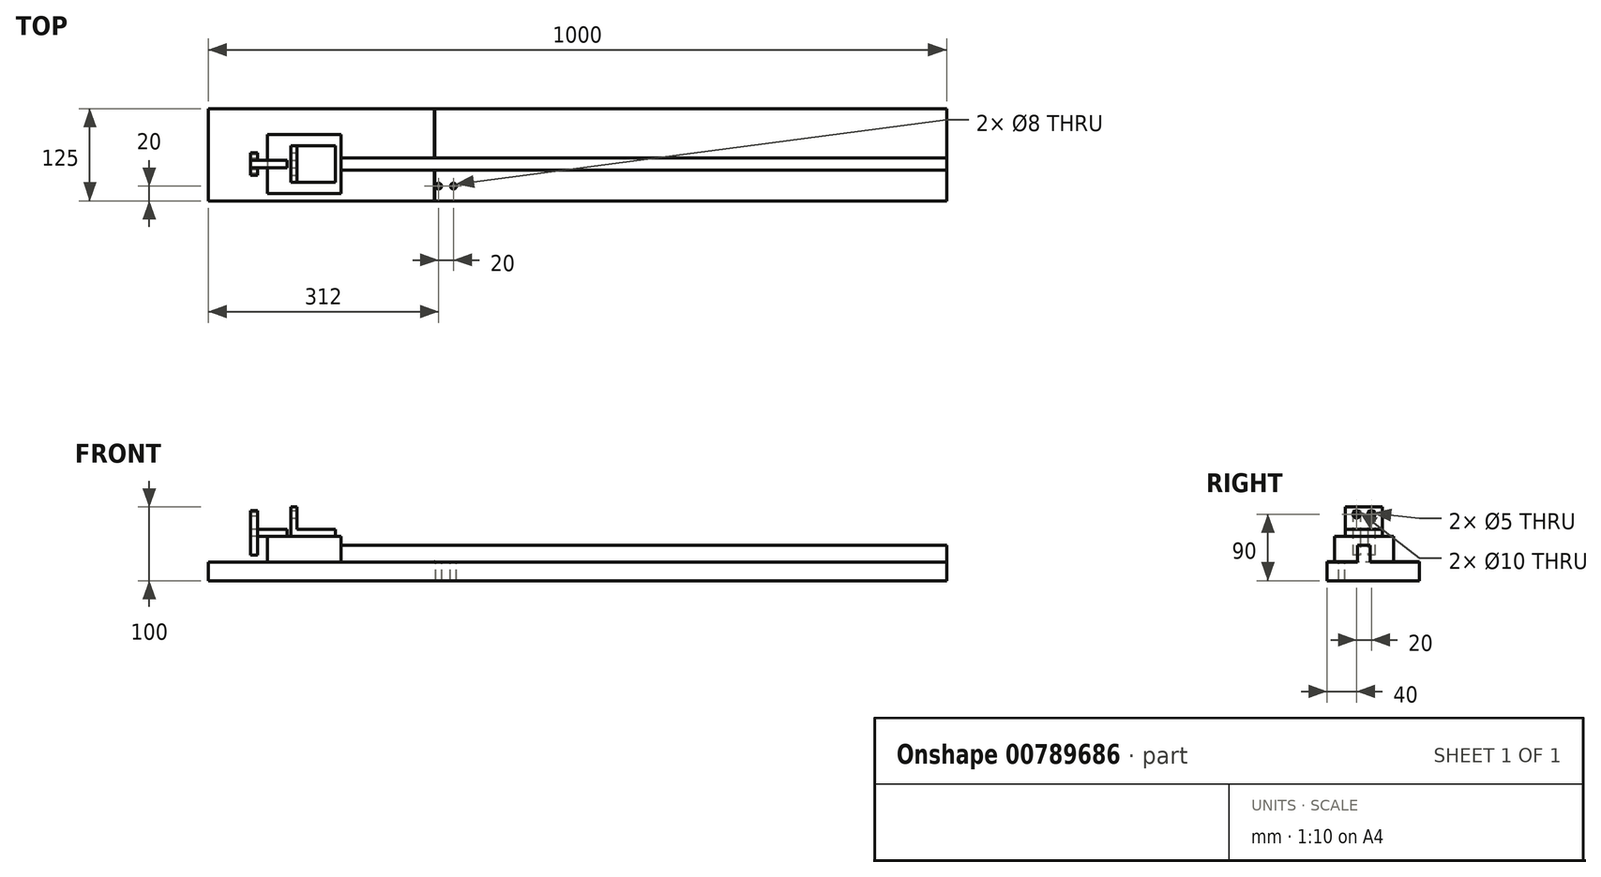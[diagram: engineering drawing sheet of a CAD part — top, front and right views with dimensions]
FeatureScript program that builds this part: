
annotation { "Feature Type Name" : "Feature", "Feature Type Description" : "" }
export const myFeature = defineFeature(function(context is Context, id is Id, definition is map)
    precondition{}
    {
        {
            var Q0;
            Q0=qCreatedBy(makeId("Top.planeOp"),FACE);
            var sketch = newSketch(context, id + "F0", { "sketchPlane" : qUnion([Q0])});
            skLineSegment(sketch, "E0.bottom", {"start": v(0, 0) * mm, "end": v(1000, 0) * mm});
            skLineSegment(sketch, "E0.top", {"start": v(0, 125) * mm, "end": v(1000, 125) * mm});
            skLineSegment(sketch, "E0.left", {"start": v(0, 0) * mm, "end": v(0, 125) * mm});
            skLineSegment(sketch, "E0.right", {"start": v(1000, 0) * mm, "end": v(1000, 125) * mm});
            skSolve(sketch);
        }
        {
            var Q0;
            Q0 = qSketchRegion(id + "F0", true);
            extrude(context, id + "F1", {"entities" : qUnion([Q0]), "depth" : 25 * mm, "offsetDistance" : 25 * mm});
        }
        {
            var Q0;
            Q0=makeQuery(id+"F1.opExtrude","CAP_FACE",FACE,{"disambiguationData":[OSD([sQuery(id+"F0.wireOp",EDGE,"E0.bottom"),sQuery(id+"F0.wireOp",EDGE,"E0.top"),sQuery(id+"F0.wireOp",EDGE,"E0.left"),sQuery(id+"F0.wireOp",EDGE,"E0.right")])],"isStart":false});
            var sketch = newSketch(context, id + "F2", { "sketchPlane" : qUnion([Q0])});
            skLineSegment(sketch, "E1.bottom", {"start": v(180, 41.5) * mm, "end": v(1000, 41.5) * mm});
            skLineSegment(sketch, "E1.top", {"start": v(180, 58.5) * mm, "end": v(1000, 58.5) * mm});
            skLineSegment(sketch, "E1.left", {"start": v(180, 41.5) * mm, "end": v(180, 58.5) * mm});
            skLineSegment(sketch, "E1.right", {"start": v(1000, 41.5) * mm, "end": v(1000, 58.5) * mm});
            skSolve(sketch);
        }
        {
            var Q0;
            Q0 = qSketchRegion(id + "F2", true);
            extrude(context, id + "F3", {"entities" : qUnion([Q0]), "operationType" : NewBodyOperationType.ADD, "depth" : 23 * mm, "offsetDistance" : 25 * mm});
        }
        {
            var Q0;
            Q0=makeQuery(id+"F1.opExtrude","CAP_FACE",FACE,{"disambiguationData":[OSD([sQuery(id+"F0.wireOp",EDGE,"E0.bottom"),sQuery(id+"F0.wireOp",EDGE,"E0.top"),sQuery(id+"F0.wireOp",EDGE,"E0.left"),sQuery(id+"F0.wireOp",EDGE,"E0.right")])],"isStart":false});
            var sketch = newSketch(context, id + "F4", { "sketchPlane" : qUnion([Q0])});
            skCircle(sketch, "E2", {"center": v(312, 20) * mm, "radius": 4 * mm});
            skCircle(sketch, "E3", {"center": v(332, 20) * mm, "radius": 4 * mm});
            skSolve(sketch);
        }
        {
            var Q0;
            Q0 = qSketchRegion(id + "F4", true);
            extrude(context, id + "F5", {"entities" : qUnion([Q0]), "operationType" : NewBodyOperationType.REMOVE, "endBound" : BoundingType.UP_TO_NEXT, "oppositeDirection" : true, "depth" : 25 * mm, "offsetDistance" : 25 * mm});
        }
        {
            var Q0;
            Q0=makeQuery(id+"F1.opExtrude","CAP_FACE",FACE,{"disambiguationData":[OSD([sQuery(id+"F0.wireOp",EDGE,"E0.bottom"),sQuery(id+"F0.wireOp",EDGE,"E0.top"),sQuery(id+"F0.wireOp",EDGE,"E0.left"),sQuery(id+"F0.wireOp",EDGE,"E0.right")])],"isStart":false});
            var sketch = newSketch(context, id + "F6", { "sketchPlane" : qUnion([Q0])});
            skLineSegment(sketch, "E4.bottom", {"start": v(80, 90) * mm, "end": v(180, 90) * mm});
            skLineSegment(sketch, "E4.top", {"start": v(80, 10) * mm, "end": v(180, 10) * mm});
            skLineSegment(sketch, "E4.left", {"start": v(80, 90) * mm, "end": v(80, 10) * mm});
            skLineSegment(sketch, "E4.right", {"start": v(180, 90) * mm, "end": v(180, 10) * mm});
            skSolve(sketch);
        }
        {
            var Q0;
            Q0 = qSketchRegion(id + "F6", true);
            extrude(context, id + "F7", {"entities" : qUnion([Q0]), "operationType" : NewBodyOperationType.ADD, "depth" : 35 * mm, "offsetDistance" : 25 * mm});
        }
        {
            var Q0;
            Q0=makeQuery(id+"F7.opExtrude","CAP_FACE",FACE,{"disambiguationData":[OSD([sQuery(id+"F6.wireOp",EDGE,"E4.bottom"),sQuery(id+"F6.wireOp",EDGE,"E4.top"),sQuery(id+"F6.wireOp",EDGE,"E4.left"),sQuery(id+"F6.wireOp",EDGE,"E4.right")])],"isStart":false});
            var sketch = newSketch(context, id + "F8", { "sketchPlane" : qUnion([Q0])});
            skLineSegment(sketch, "E5.bottom", {"start": v(107, 45) * mm, "end": v(57, 45) * mm});
            skLineSegment(sketch, "E5.top", {"start": v(107, 55) * mm, "end": v(57, 55) * mm});
            skLineSegment(sketch, "E5.left", {"start": v(107, 45) * mm, "end": v(107, 55) * mm});
            skLineSegment(sketch, "E5.right", {"start": v(57, 45) * mm, "end": v(57, 55) * mm});
            skSolve(sketch);
        }
        {
            var Q0;
            Q0 = qSketchRegion(id + "F8", true);
            extrude(context, id + "F9", {"entities" : qUnion([Q0]), "operationType" : NewBodyOperationType.ADD, "depth" : 10 * mm, "offsetDistance" : 25 * mm});
        }
        {
            var Q0;
            Q0=makeQuery(id+"F9.opExtrude","SWEPT_FACE",FACE,{"disambiguationData":[OSD([sQuery(id+"F8.wireOp",EDGE,"E5.right")])]});
            var sketch = newSketch(context, id + "F10", { "sketchPlane" : qUnion([Q0])});
            skLineSegment(sketch, "E6.bottom", {"start": v(-65, 95) * mm, "end": v(-55, 95) * mm});
            skLineSegment(sketch, "E6.top", {"start": v(-65, 35) * mm, "end": v(-55, 35) * mm});
            skLineSegment(sketch, "E6.left", {"start": v(-65, 95) * mm, "end": v(-65, 35) * mm});
            skLineSegment(sketch, "E6.right", {"start": v(-55, 95) * mm, "end": v(-55, 35) * mm});
            skLineSegment(sketch, "E7.bottom", {"start": v(-45, 95) * mm, "end": v(-35, 95) * mm});
            skLineSegment(sketch, "E7.top", {"start": v(-45, 35) * mm, "end": v(-35, 35) * mm});
            skLineSegment(sketch, "E7.left", {"start": v(-45, 95) * mm, "end": v(-45, 35) * mm});
            skLineSegment(sketch, "E7.right", {"start": v(-35, 95) * mm, "end": v(-35, 35) * mm});
            skCircle(sketch, "E8", {"center": v(-60, 90) * mm, "radius": 2.5 * mm});
            skCircle(sketch, "E9", {"center": v(-40, 90) * mm, "radius": 2.5 * mm});
            skSolve(sketch);
        }
        {
            var Q0;
            Q0 = qSketchRegion(id + "F10", true);
            extrude(context, id + "F11", {"entities" : qUnion([Q0]), "operationType" : NewBodyOperationType.ADD, "oppositeDirection" : true, "depth" : 10 * mm, "offsetDistance" : 25 * mm});
        }
        {
            var Q0;
            Q0=makeQuery(id+"F9.opExtrude","SWEPT_FACE",FACE,{"disambiguationData":[OSD([sQuery(id+"F8.wireOp",EDGE,"E5.bottom")])]});
            var sketch = newSketch(context, id + "F12", { "sketchPlane" : qUnion([Q0])});
            skLineSegment(sketch, "E10", {"start": v(172, 60) * mm, "end": v(112, 60) * mm});
            skLineSegment(sketch, "E11", {"start": v(112, 60) * mm, "end": v(112, 100) * mm});
            skLineSegment(sketch, "E12", {"start": v(112, 100) * mm, "end": v(120, 100) * mm});
            skLineSegment(sketch, "E13", {"start": v(120, 100) * mm, "end": v(120, 70) * mm});
            skLineSegment(sketch, "E14", {"start": v(120, 70) * mm, "end": v(172, 70) * mm});
            skLineSegment(sketch, "E15", {"start": v(172, 70) * mm, "end": v(172, 60) * mm});
            skSolve(sketch);
        }
        {
            var Q0;
            Q0 = qSketchRegion(id + "F12", true);
            extrude(context, id + "F13", {"entities" : qUnion([Q0]), "operationType" : NewBodyOperationType.ADD, "depth" : 20 * mm, "offsetDistance" : 25 * mm, "hasSecondDirection" : true, "secondDirectionOppositeDirection" : true, "secondDirectionDepth" : 30 * mm});
        }
        {
            var Q0;
            Q0=makeQuery(id+"F13.opExtrude","SWEPT_FACE",FACE,{"disambiguationData":[OSD([sQuery(id+"F12.wireOp",EDGE,"E13")])]});
            var sketch = newSketch(context, id + "F14", { "sketchPlane" : qUnion([Q0])});
            skCircle(sketch, "E16", {"center": v(40, 90) * mm, "radius": 5 * mm});
            skCircle(sketch, "E17", {"center": v(60, 90) * mm, "radius": 5 * mm});
            skSolve(sketch);
        }
        {
            var Q0;
            Q0 = qSketchRegion(id + "F14", true);
            extrude(context, id + "F15", {"entities" : qUnion([Q0]), "operationType" : NewBodyOperationType.REMOVE, "oppositeDirection" : true, "depth" : 25 * mm, "offsetDistance" : 25 * mm});
        }
        {
            var Q0;
            Q0=makeQuery(id+"F1.opExtrude","CAP_FACE",FACE,{"disambiguationData":[OSD([sQuery(id+"F0.wireOp",EDGE,"E0.bottom"),sQuery(id+"F0.wireOp",EDGE,"E0.top"),sQuery(id+"F0.wireOp",EDGE,"E0.left"),sQuery(id+"F0.wireOp",EDGE,"E0.right")])],"isStart":false});
            var sketch = newSketch(context, id + "F16", { "sketchPlane" : qUnion([Q0])});
            skLineSegment(sketch, "E18", {"start": v(297, 40) * mm, "end": v(307, 40) * mm});
            skLineSegment(sketch, "E19", {"start": v(307, 40) * mm, "end": v(307, 32) * mm});
            skLineSegment(sketch, "E20", {"start": v(307, 32) * mm, "end": v(347, 32) * mm});
            skLineSegment(sketch, "E21", {"start": v(347, 32) * mm, "end": v(347, -10) * mm});
            skLineSegment(sketch, "E22", {"start": v(347, -10) * mm, "end": v(297, -10) * mm});
            skLineSegment(sketch, "E23", {"start": v(297, -10) * mm, "end": v(297, 40) * mm});
            skLineSegment(sketch, "E24.bottom", {"start": v(307, 24.25) * mm, "end": v(337, 24.25) * mm});
            skLineSegment(sketch, "E24.top", {"start": v(307, 15.75) * mm, "end": v(337, 15.75) * mm});
            skArc(sketch, "E25", {"start": v(307, 24.25) * mm, "mid": v(302.75, 20) * mm, "end": v(307, 15.75) * mm});
            skArc(sketch, "E26", {"start": v(337, 15.75) * mm, "mid": v(341.25, 20) * mm, "end": v(337, 24.25) * mm});
            skSolve(sketch);
        }
        {
            var Q0;
            {var subQ13=sQuery(id+"F16.wireOp",EDGE,"E18");Q0=makeQuery(id+"F16.imprint","IMPRINT",FACE,{"disambiguationData":[TD([[makeQuery(id+"F16.imprint","IMPRINT",EDGE,{"derivedFrom":subQ13}),1.0]])]});}
            var sketch = newSketch(context, id + "F17", { "sketchPlane" : qUnion([Q0])});
            skLineSegment(sketch, "E27.bottom", {"start": v(307, 125) * mm, "end": v(306, 125) * mm});
            skLineSegment(sketch, "E27.top", {"start": v(307, 0) * mm, "end": v(306, 0) * mm});
            skLineSegment(sketch, "E27.left", {"start": v(307, 125) * mm, "end": v(307, 0) * mm});
            skLineSegment(sketch, "E27.right", {"start": v(306, 125) * mm, "end": v(306, 0) * mm});
            skSolve(sketch);
        }
        {
            var Q0;
            Q0 = qSketchRegion(id + "F17", true);
            extrude(context, id + "F18", {"entities" : qUnion([Q0]), "operationType" : NewBodyOperationType.ADD, "depth" : 1 * mm, "offsetDistance" : 25 * mm});
        }
    });
